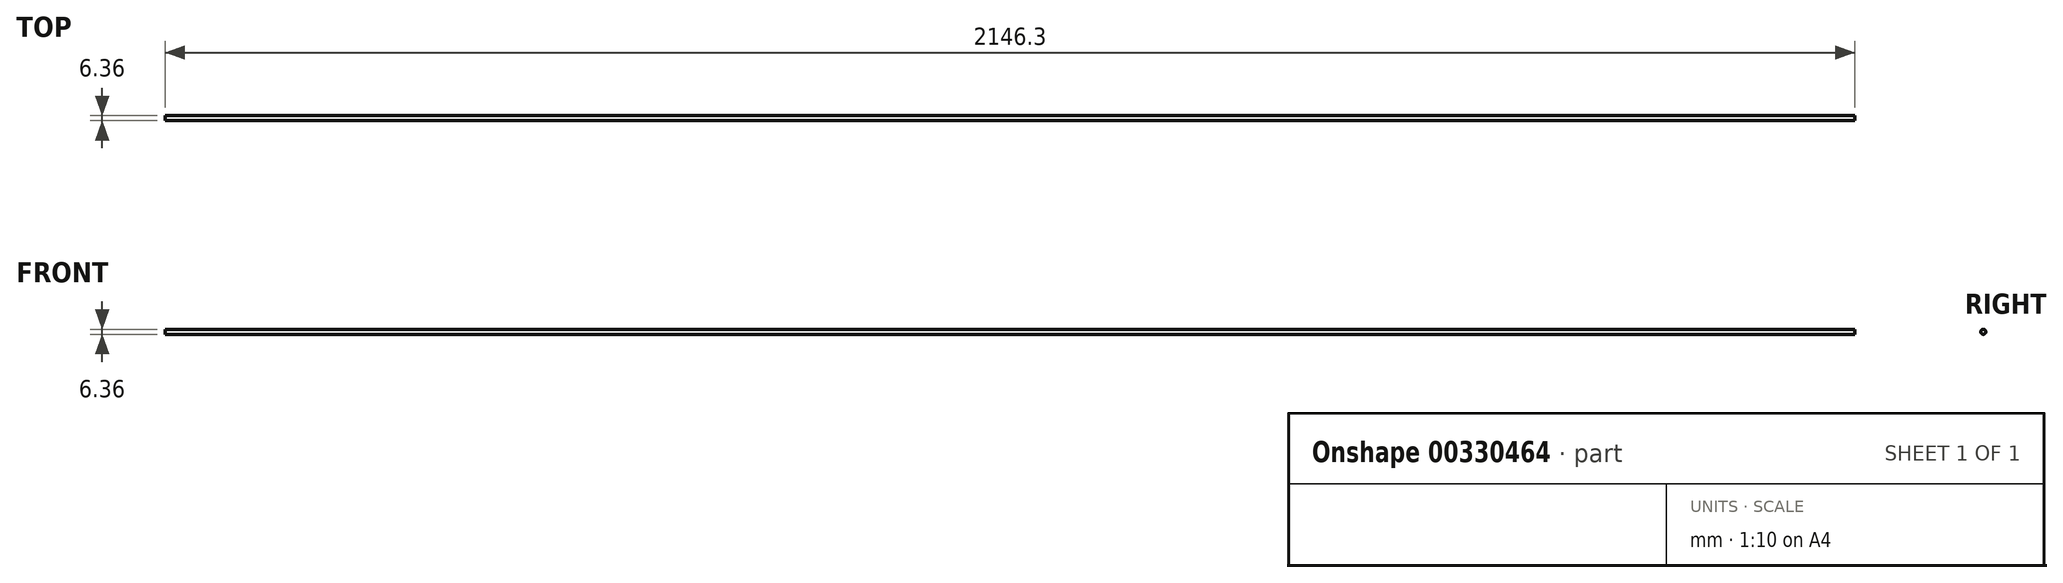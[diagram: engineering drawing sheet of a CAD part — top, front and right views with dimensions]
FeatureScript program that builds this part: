
annotation { "Feature Type Name" : "Feature", "Feature Type Description" : "" }
export const myFeature = defineFeature(function(context is Context, id is Id, definition is map)
    precondition{}
    {
        {
            var Q0;
            Q0=qCreatedBy(makeId("Right.planeOp"),FACE);
            var sketch = newSketch(context, id + "F0", { "sketchPlane" : qUnion([Q0])});
            skCircle(sketch, "E0", {"center": v(0, 0) * mm, "radius": 3.18 * mm});
            skSolve(sketch);
        }
        {
            var Q0;
            Q0=makeQuery(id+"F0.imprint","IMPRINT",FACE,{"disambiguationData":[TD([[makeQuery(id+"F0.imprint","IMPRINT",EDGE,{"derivedFrom":sQuery(id+"F0.wireOp",EDGE,"E0")}),1.0]])]});
            extrude(context, id + "F1", {"entities" : qUnion([Q0]), "depth" : 2146.3 * mm});
        }
    });
